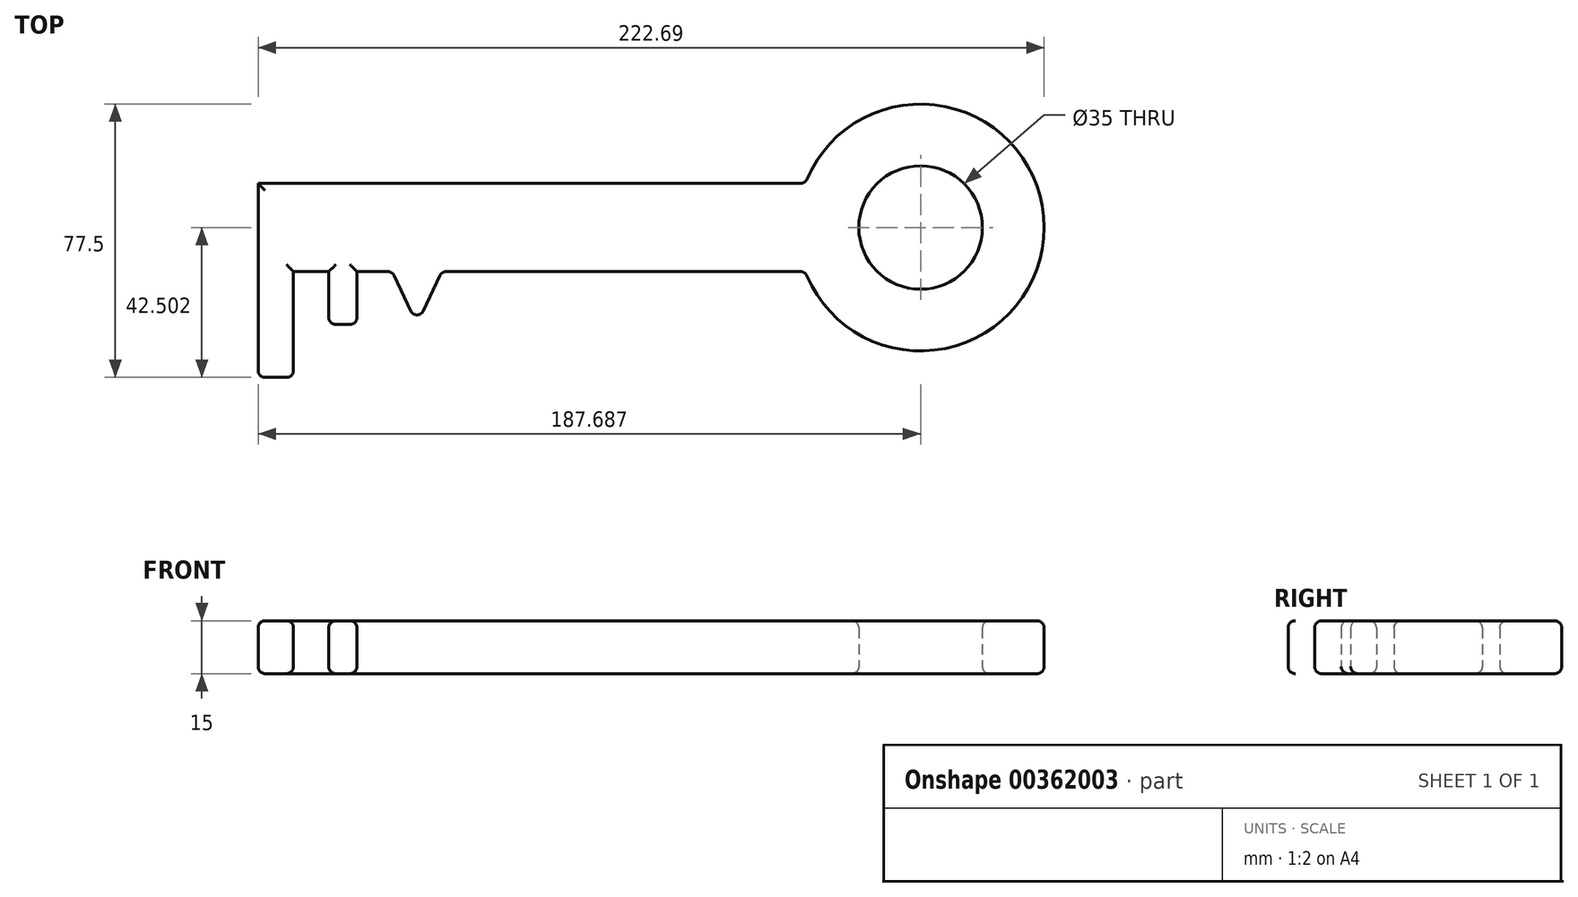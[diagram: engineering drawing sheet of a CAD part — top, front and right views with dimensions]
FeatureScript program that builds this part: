
annotation { "Feature Type Name" : "Feature", "Feature Type Description" : "" }
export const myFeature = defineFeature(function(context is Context, id is Id, definition is map)
    precondition{}
    {
        {
            var Q0;
            Q0=qCreatedBy(makeId("Top.planeOp"),FACE);
            var sketch = newSketch(context, id + "F0", { "sketchPlane" : qUnion([Q0])});
            skLineSegment(sketch, "E0.bottom", {"start": v(-155.71, 25.35) * mm, "end": v(-0.71, 25.35) * mm});
            skLineSegment(sketch, "E0.top", {"start": v(-155.71, 0.35) * mm, "end": v(-0.71, 0.35) * mm});
            skLineSegment(sketch, "E0.left", {"start": v(-155.71, 25.35) * mm, "end": v(-155.71, 0.35) * mm});
            skLineSegment(sketch, "E1.bottom", {"start": v(-155.71, 0.35) * mm, "end": v(-145.71, 0.35) * mm});
            skLineSegment(sketch, "E1.top", {"start": v(-155.71, -29.65) * mm, "end": v(-145.71, -29.65) * mm});
            skLineSegment(sketch, "E1.left", {"start": v(-155.71, 0.35) * mm, "end": v(-155.71, -29.65) * mm});
            skLineSegment(sketch, "E1.right", {"start": v(-145.71, 0.35) * mm, "end": v(-145.71, -29.65) * mm});
            skLineSegment(sketch, "E2.bottom", {"start": v(-135.71, 0.35) * mm, "end": v(-127.71, 0.35) * mm});
            skLineSegment(sketch, "E2.top", {"start": v(-135.71, -14.65) * mm, "end": v(-127.71, -14.65) * mm});
            skLineSegment(sketch, "E2.left", {"start": v(-135.71, 0.35) * mm, "end": v(-135.71, -14.65) * mm});
            skLineSegment(sketch, "E2.right", {"start": v(-127.71, 0.35) * mm, "end": v(-127.71, -14.65) * mm});
            skLineSegment(sketch, "E3", {"start": v(-117.71, 0.35) * mm, "end": v(-110.71, -14.65) * mm});
            skLineSegment(sketch, "E4", {"start": v(-110.71, -14.65) * mm, "end": v(-103.71, 0.35) * mm});
            skArc(sketch, "E5", {"start": v(-0.71, 0.35) * mm, "mid": v(66.98, 12.85) * mm, "end": v(-0.71, 25.35) * mm});
            skCircle(sketch, "E6", {"center": v(31.98, 12.85) * mm, "radius": 17.5 * mm});
            skLineSegment(sketch, "E7", {"start": v(31.98, 12.85) * mm, "end": v(-155.71, 12.85) * mm});
            skSolve(sketch);
        }
        {
            var Q0;
            Q0 = qSketchRegion(id + "F0", true);
            extrude(context, id + "F1", {"entities" : qUnion([Q0]), "depth" : 15 * mm});
        }
        {
            var Q0;
            Q0=makeQuery(id+"F1.opExtrude","CAP_EDGE",EDGE,{"disambiguationData":[OSD([sQuery(id+"F0.wireOp",EDGE,"E6")])],"isStart":false});
            var Q1;
            Q1=makeQuery(id+"F1.opExtrude","CAP_FACE",FACE,{"disambiguationData":[OSD([sQuery(id+"F0.wireOp",EDGE,"E0.bottom"),sQuery(id+"F0.wireOp",EDGE,"E0.top"),sQuery(id+"F0.wireOp",EDGE,"E0.left"),sQuery(id+"F0.wireOp",EDGE,"E1.top"),sQuery(id+"F0.wireOp",EDGE,"E1.left"),sQuery(id+"F0.wireOp",EDGE,"E1.right"),sQuery(id+"F0.wireOp",EDGE,"E2.top"),sQuery(id+"F0.wireOp",EDGE,"E2.left"),sQuery(id+"F0.wireOp",EDGE,"E2.right"),sQuery(id+"F0.wireOp",EDGE,"E3"),sQuery(id+"F0.wireOp",EDGE,"E4"),sQuery(id+"F0.wireOp",EDGE,"E5"),sQuery(id+"F0.wireOp",EDGE,"E6")])],"isStart":false});
            var Q2;
            {var subQ0=sQuery(id+"F0.wireOp",EDGE,"E0.top");Q2=makeQuery(id+"F1.opExtrude","CAP_EDGE",EDGE,{"disambiguationData":[OSD([subQ0]),TDD([makeQuery(id+"F0.imprint","IMPRINT",EDGE,{"disambiguationData":[TD([[makeQuery(id+"F0.imprint","INTERSECT",VERTEX,{"derivedFrom":[subQ0,sQuery(id+"F0.wireOp",EDGE,"E5")]}),1.0]])],"derivedFrom":subQ0})])],"isStart":false});}
            var Q3;
            Q3=makeQuery(id+"F1.opExtrude","CAP_EDGE",EDGE,{"disambiguationData":[OSD([sQuery(id+"F0.wireOp",EDGE,"E0.bottom")])],"isStart":false});
            var Q4;
            Q4=makeQuery(id+"F1.opExtrude","CAP_EDGE",EDGE,{"disambiguationData":[OSD([sQuery(id+"F0.wireOp",EDGE,"E1.top")])],"isStart":false});
            var Q5;
            Q5=makeQuery(id+"F1.opExtrude","CAP_EDGE",EDGE,{"disambiguationData":[OSD([sQuery(id+"F0.wireOp",EDGE,"E6")])],"isStart":true});
            var Q6;
            {var subQ0=sQuery(id+"F0.wireOp",EDGE,"E0.top");Q6=makeQuery(id+"F1.opExtrude","CAP_EDGE",EDGE,{"disambiguationData":[OSD([subQ0]),TDD([makeQuery(id+"F0.imprint","IMPRINT",EDGE,{"disambiguationData":[TD([[makeQuery(id+"F0.imprint","INTERSECT",VERTEX,{"derivedFrom":[subQ0,sQuery(id+"F0.wireOp",EDGE,"E5")]}),1.0]])],"derivedFrom":subQ0})])],"isStart":true});}
            var Q7;
            Q7=makeQuery(id+"F1.opExtrude","CAP_EDGE",EDGE,{"disambiguationData":[OSD([sQuery(id+"F0.wireOp",EDGE,"E5")])],"isStart":true});
            var Q8;
            Q8=makeQuery(id+"F1.opExtrude","CAP_EDGE",EDGE,{"disambiguationData":[OSD([sQuery(id+"F0.wireOp",EDGE,"E0.bottom")])],"isStart":true});
            var Q9;
            Q9=makeQuery(id+"F1.opExtrude","SWEPT_EDGE",EDGE,{"disambiguationData":[OSD([sQuery(id+"F0.wireOp",EDGE,"E1.top"),sQuery(id+"F0.wireOp",EDGE,"E1.right")])]});
            var Q10;
            Q10=makeQuery(id+"F1.opExtrude","SWEPT_EDGE",EDGE,{"disambiguationData":[OSD([sQuery(id+"F0.wireOp",EDGE,"E1.top"),sQuery(id+"F0.wireOp",EDGE,"E1.left")])]});
            var Q11;
            Q11=makeQuery(id+"F1.opExtrude","CAP_EDGE",EDGE,{"disambiguationData":[OSD([sQuery(id+"F0.wireOp",EDGE,"E1.top")])],"isStart":true});
            var Q12;
            {var subQ0=sQuery(id+"F0.wireOp",EDGE,"E0.top");Q12=makeQuery(id+"F1.opExtrude","CAP_EDGE",EDGE,{"disambiguationData":[OSD([subQ0]),TDD([makeQuery(id+"F0.imprint","IMPRINT",EDGE,{"disambiguationData":[TD([[makeQuery(id+"F0.imprint","INTERSECT",VERTEX,{"derivedFrom":[subQ0,sQuery(id+"F0.wireOp",EDGE,"E1.bottom"),sQuery(id+"F0.wireOp",EDGE,"E1.right")]}),-1.0]])],"derivedFrom":subQ0})])],"isStart":true});}
            var Q13;
            Q13=makeQuery(id+"F1.opExtrude","SWEPT_EDGE",EDGE,{"disambiguationData":[OSD([sQuery(id+"F0.wireOp",EDGE,"E2.top"),sQuery(id+"F0.wireOp",EDGE,"E2.left")])]});
            var Q14;
            Q14=makeQuery(id+"F1.opExtrude","CAP_EDGE",EDGE,{"disambiguationData":[OSD([sQuery(id+"F0.wireOp",EDGE,"E2.top")])],"isStart":true});
            var Q15;
            Q15=makeQuery(id+"F1.opExtrude","SWEPT_EDGE",EDGE,{"disambiguationData":[OSD([sQuery(id+"F0.wireOp",EDGE,"E2.top"),sQuery(id+"F0.wireOp",EDGE,"E2.right")])]});
            var Q16;
            Q16=makeQuery(id+"F1.opExtrude","CAP_EDGE",EDGE,{"disambiguationData":[OSD([sQuery(id+"F0.wireOp",EDGE,"E3")])],"isStart":true});
            var Q17;
            Q17=makeQuery(id+"F1.opExtrude","SWEPT_EDGE",EDGE,{"disambiguationData":[OSD([sQuery(id+"F0.wireOp",EDGE,"E0.top"),sQuery(id+"F0.wireOp",EDGE,"E3")])]});
            var Q18;
            Q18=makeQuery(id+"F1.opExtrude","SWEPT_EDGE",EDGE,{"disambiguationData":[OSD([sQuery(id+"F0.wireOp",EDGE,"E0.top"),sQuery(id+"F0.wireOp",EDGE,"E4")])]});
            var Q19;
            Q19=makeQuery(id+"F1.opExtrude","SWEPT_EDGE",EDGE,{"disambiguationData":[OSD([sQuery(id+"F0.wireOp",EDGE,"E3"),sQuery(id+"F0.wireOp",EDGE,"E4")])]});
            var Q20;
            Q20=makeQuery(id+"F1.opExtrude","CAP_EDGE",EDGE,{"disambiguationData":[OSD([sQuery(id+"F0.wireOp",EDGE,"E5")])],"isStart":false});
            var Q21;
            Q21=makeQuery(id+"F1.opExtrude","SWEPT_EDGE",EDGE,{"disambiguationData":[OSD([sQuery(id+"F0.wireOp",EDGE,"E0.bottom"),sQuery(id+"F0.wireOp",EDGE,"E5")])]});
            var Q22;
            Q22=makeQuery(id+"F1.opExtrude","SWEPT_FACE",FACE,{"disambiguationData":[OSD([sQuery(id+"F0.wireOp",EDGE,"E5")])]});
            var Q23;
            Q23=makeQuery(id+"F1.opExtrude","CAP_EDGE",EDGE,{"disambiguationData":[OSD([sQuery(id+"F0.wireOp",EDGE,"E4")])],"isStart":true});
            var Q24;
            Q24=makeQuery(id+"F1.opExtrude","CAP_FACE",FACE,{"disambiguationData":[OSD([sQuery(id+"F0.wireOp",EDGE,"E0.bottom"),sQuery(id+"F0.wireOp",EDGE,"E0.top"),sQuery(id+"F0.wireOp",EDGE,"E0.left"),sQuery(id+"F0.wireOp",EDGE,"E1.top"),sQuery(id+"F0.wireOp",EDGE,"E1.left"),sQuery(id+"F0.wireOp",EDGE,"E1.right"),sQuery(id+"F0.wireOp",EDGE,"E2.top"),sQuery(id+"F0.wireOp",EDGE,"E2.left"),sQuery(id+"F0.wireOp",EDGE,"E2.right"),sQuery(id+"F0.wireOp",EDGE,"E3"),sQuery(id+"F0.wireOp",EDGE,"E4"),sQuery(id+"F0.wireOp",EDGE,"E5"),sQuery(id+"F0.wireOp",EDGE,"E6")])],"isStart":true});
            fillet(context, id + "F2", {"entities" : qUnion([Q0, Q1, Q2, Q3, Q4, Q5, Q6, Q7, Q8, Q9, Q10, Q11, Q12, Q13, Q14, Q15, Q16, Q17, Q18, Q19, Q20, Q21, Q22, Q23, Q24]), "radius" : 2 * mm, "tangentPropagation" : true, "allowEdgeOverflow" : false});
        }
    });
